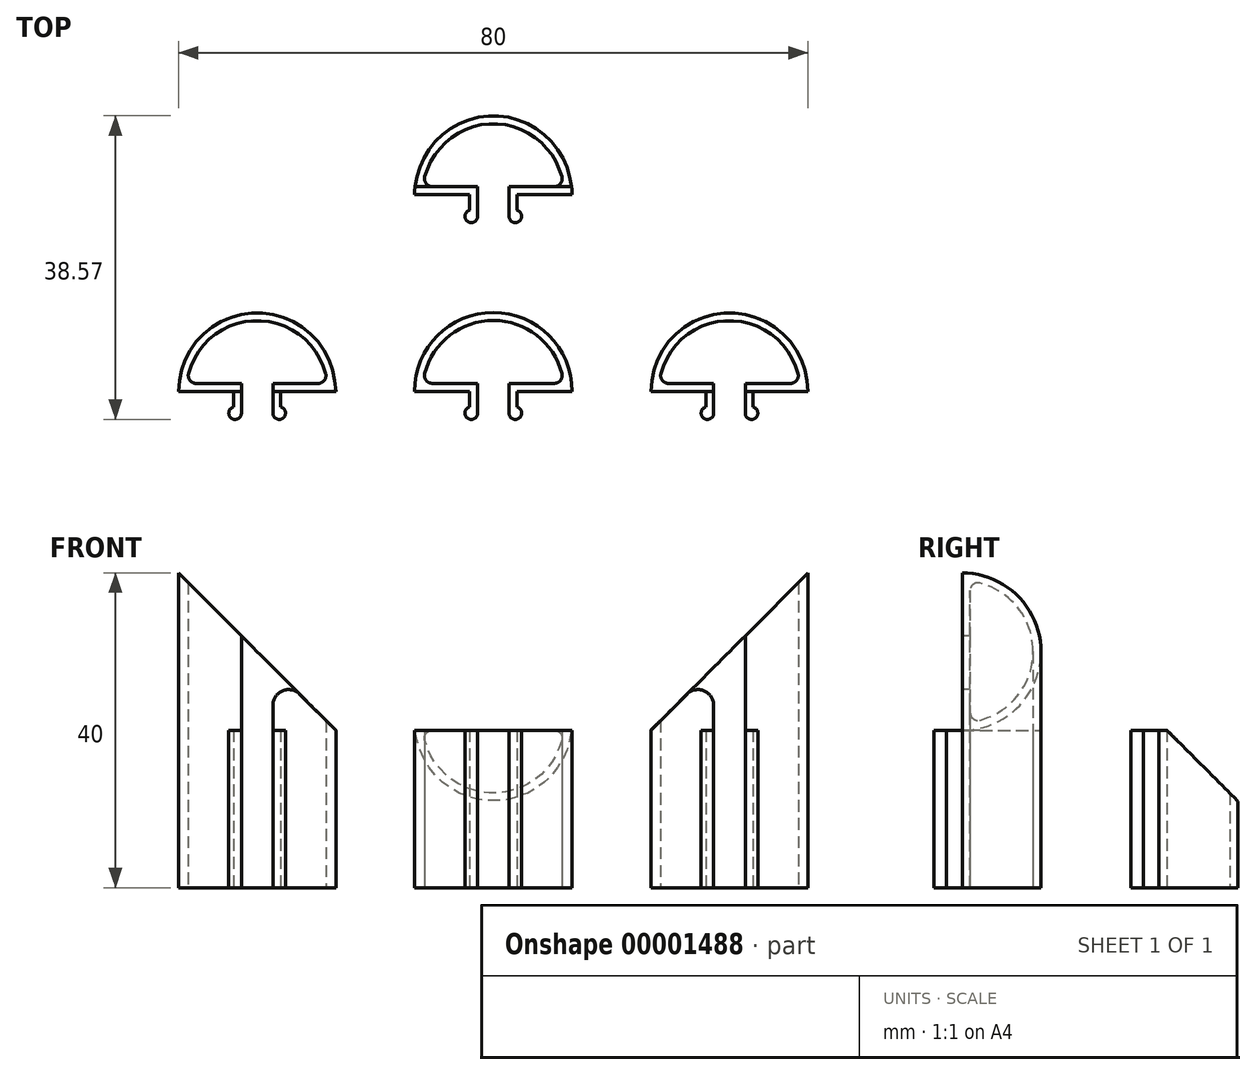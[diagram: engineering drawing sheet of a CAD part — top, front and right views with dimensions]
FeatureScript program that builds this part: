
annotation { "Feature Type Name" : "Feature", "Feature Type Description" : "" }
export const myFeature = defineFeature(function(context is Context, id is Id, definition is map)
    precondition{}
    {
        {
            var Q0;
            Q0=qCreatedBy(makeId("Top.planeOp"),FACE);
            var sketch = newSketch(context, id + "F0", { "sketchPlane" : qUnion([Q0])});
            skLineSegment(sketch, "E0", {"start": v(-3, 0) * mm, "end": v(-10, 0) * mm});
            skLineSegment(sketch, "E1", {"start": v(3, 0) * mm, "end": v(10, 0) * mm});
            skLineSegment(sketch, "E2", {"start": v(-3, 0) * mm, "end": v(-3, -2) * mm});
            skLineSegment(sketch, "E3", {"start": v(3, -2) * mm, "end": v(3, 0) * mm});
            skArc(sketch, "E4", {"start": v(10, 0) * mm, "mid": v(0, 10) * mm, "end": v(-10, 0) * mm});
            skLineSegment(sketch, "E5.0", {"start": v(-2, 1) * mm, "end": v(-2, -2.77) * mm});
            skLineSegment(sketch, "E5.1", {"start": v(-2, 1) * mm, "end": v(-8.94, 1) * mm});
            skArc(sketch, "E5.2", {"start": v(8.94, 1) * mm, "mid": v(0, 9) * mm, "end": v(-8.94, 1) * mm});
            skLineSegment(sketch, "E5.3", {"start": v(2, 1) * mm, "end": v(8.94, 1) * mm});
            skLineSegment(sketch, "E5.4", {"start": v(2, -2.77) * mm, "end": v(2, 1) * mm});
            skArc(sketch, "E6", {"start": v(-2, -2.77) * mm, "mid": v(-3.29, -3.4) * mm, "end": v(-3, -2) * mm});
            skArc(sketch, "E7", {"start": v(2, -2.77) * mm, "mid": v(3.29, -3.4) * mm, "end": v(3, -2) * mm});
            skLineSegment(sketch, "E8", {"start": v(-2.8, -2.77) * mm, "end": v(-3.6, -2.77) * mm, "construction": true});
            skLineSegment(sketch, "E9", {"start": v(2.8, -2.77) * mm, "end": v(3.6, -2.77) * mm, "construction": true});
            skSolve(sketch);
        }
        {
            var Q0;
            Q0 = qSketchRegion(id + "F0", true);
            extrude(context, id + "F1", {"entities" : qUnion([Q0]), "depth" : 20 * mm});
        }
        {
            var Q0;
            Q0=makeQuery(id+"F1.opExtrude","SWEPT_BODY",BODY,{"disambiguationData":[OSD([sQuery(id+"F0.wireOp",EDGE,"E0"),sQuery(id+"F0.wireOp",EDGE,"E1"),sQuery(id+"F0.wireOp",EDGE,"E2"),sQuery(id+"F0.wireOp",EDGE,"E3"),sQuery(id+"F0.wireOp",EDGE,"E4"),sQuery(id+"F0.wireOp",EDGE,"E5.0"),sQuery(id+"F0.wireOp",EDGE,"E5.1"),sQuery(id+"F0.wireOp",EDGE,"E5.2"),sQuery(id+"F0.wireOp",EDGE,"E5.3"),sQuery(id+"F0.wireOp",EDGE,"E5.4"),sQuery(id+"F0.wireOp",EDGE,"E6"),sQuery(id+"F0.wireOp",EDGE,"E7")])]});
            transform(context, id + "F2", {"entities" : qUnion([Q0]), "transformType" : TransformType.TRANSLATION_3D, "dx" : 30 * mm, "dy" : 0 * mm, "dz" : 0 * mm, "makeCopy" : true});
        }
        {
            var Q0;
            Q0=makeQuery(id+"F2.opPattern","COPY",FACE,{"derivedFrom":makeQuery(id+"F1.opExtrude","CAP_FACE",FACE,{"disambiguationData":[OSD([sQuery(id+"F0.wireOp",EDGE,"E0"),sQuery(id+"F0.wireOp",EDGE,"E1"),sQuery(id+"F0.wireOp",EDGE,"E2"),sQuery(id+"F0.wireOp",EDGE,"E3"),sQuery(id+"F0.wireOp",EDGE,"E4"),sQuery(id+"F0.wireOp",EDGE,"E5.0"),sQuery(id+"F0.wireOp",EDGE,"E5.1"),sQuery(id+"F0.wireOp",EDGE,"E5.2"),sQuery(id+"F0.wireOp",EDGE,"E5.3"),sQuery(id+"F0.wireOp",EDGE,"E5.4"),sQuery(id+"F0.wireOp",EDGE,"E6"),sQuery(id+"F0.wireOp",EDGE,"E7")])],"isStart":false}),"instanceName":"1"});
            var sketch = newSketch(context, id + "F3", { "sketchPlane" : qUnion([Q0])});
            skLineSegment(sketch, "E10", {"start": v(20, 0) * mm, "end": v(28, 0) * mm});
            skLineSegment(sketch, "E11", {"start": v(28, 0) * mm, "end": v(28, 1) * mm});
            skLineSegment(sketch, "E12", {"start": v(40, 0) * mm, "end": v(32, 0) * mm});
            skLineSegment(sketch, "E13", {"start": v(32, 0) * mm, "end": v(32, 1) * mm});
            skLineSegment(sketch, "E14.0", {"start": v(28, 1) * mm, "end": v(21.06, 1) * mm});
            skArc(sketch, "E15.0", {"start": v(38.94, 1) * mm, "mid": v(30, 9) * mm, "end": v(21.06, 1) * mm});
            skArc(sketch, "E16.0", {"start": v(40, 0) * mm, "mid": v(30, 10) * mm, "end": v(20, 0) * mm});
            skLineSegment(sketch, "E17.0", {"start": v(32, 1) * mm, "end": v(38.94, 1) * mm});
            skSolve(sketch);
        }
        {
            var Q0;
            Q0 = qSketchRegion(id + "F3", true);
            extrude(context, id + "F4", {"entities" : qUnion([Q0]), "operationType" : NewBodyOperationType.ADD, "depth" : 20 * mm});
        }
        {
            var Q0;
            Q0=makeQuery(id+"F4.boolean.opBoolean","MERGE",FACE,{"derivedFrom":[makeQuery(id+"F2.opPattern","COPY",FACE,{"derivedFrom":makeQuery(id+"F1.opExtrude","SWEPT_FACE",FACE,{"disambiguationData":[OSD([sQuery(id+"F0.wireOp",EDGE,"E1")])]}),"instanceName":"1"}),makeQuery(id+"F4.opExtrude","SWEPT_FACE",FACE,{"disambiguationData":[OSD([sQuery(id+"F3.wireOp",EDGE,"E12")])]})]});
            var sketch = newSketch(context, id + "F5", { "sketchPlane" : qUnion([Q0])});
            skLineSegment(sketch, "E18", {"start": v(40, 40) * mm, "end": v(20, 40) * mm});
            skLineSegment(sketch, "E19", {"start": v(20, 40) * mm, "end": v(20, 20) * mm});
            skLineSegment(sketch, "E20", {"start": v(20, 20) * mm, "end": v(40, 40) * mm});
            skSolve(sketch);
        }
        {
            var Q0;
            Q0 = qSketchRegion(id + "F5", true);
            extrude(context, id + "F6", {"entities" : qUnion([Q0]), "operationType" : NewBodyOperationType.REMOVE, "endBound" : BoundingType.THROUGH_ALL, "oppositeDirection" : true, "depth" : 25 * mm});
        }
        {
            var Q0;
            Q0=makeQuery(id+"F2.opPattern","COPY",BODY,{"derivedFrom":makeQuery(id+"F1.opExtrude","SWEPT_BODY",BODY,{"disambiguationData":[OSD([sQuery(id+"F0.wireOp",EDGE,"E0"),sQuery(id+"F0.wireOp",EDGE,"E1"),sQuery(id+"F0.wireOp",EDGE,"E2"),sQuery(id+"F0.wireOp",EDGE,"E3"),sQuery(id+"F0.wireOp",EDGE,"E4"),sQuery(id+"F0.wireOp",EDGE,"E5.0"),sQuery(id+"F0.wireOp",EDGE,"E5.1"),sQuery(id+"F0.wireOp",EDGE,"E5.2"),sQuery(id+"F0.wireOp",EDGE,"E5.3"),sQuery(id+"F0.wireOp",EDGE,"E5.4"),sQuery(id+"F0.wireOp",EDGE,"E6"),sQuery(id+"F0.wireOp",EDGE,"E7")])]}),"instanceName":"1"});
            var Q1;
            Q1=qCreatedBy(makeId("Right.planeOp"),FACE);
            mirror(context, id + "F7", {"entities" : qUnion([Q0]), "mirrorPlane" : qUnion([Q1])});
        }
        {
            var Q0;
            Q0=makeQuery(id+"F1.opExtrude","SWEPT_BODY",BODY,{"disambiguationData":[OSD([sQuery(id+"F0.wireOp",EDGE,"E0"),sQuery(id+"F0.wireOp",EDGE,"E1"),sQuery(id+"F0.wireOp",EDGE,"E2"),sQuery(id+"F0.wireOp",EDGE,"E3"),sQuery(id+"F0.wireOp",EDGE,"E4"),sQuery(id+"F0.wireOp",EDGE,"E5.0"),sQuery(id+"F0.wireOp",EDGE,"E5.1"),sQuery(id+"F0.wireOp",EDGE,"E5.2"),sQuery(id+"F0.wireOp",EDGE,"E5.3"),sQuery(id+"F0.wireOp",EDGE,"E5.4"),sQuery(id+"F0.wireOp",EDGE,"E6"),sQuery(id+"F0.wireOp",EDGE,"E7")])]});
            transform(context, id + "F8", {"entities" : qUnion([Q0]), "transformType" : TransformType.TRANSLATION_3D, "dx" : 0 * mm, "dy" : 25 * mm, "dz" : 0 * mm, "makeCopy" : true});
        }
        {
            var Q0;
            Q0=makeQuery(id+"F8.opPattern","COPY",FACE,{"derivedFrom":makeQuery(id+"F1.opExtrude","SWEPT_FACE",FACE,{"disambiguationData":[OSD([sQuery(id+"F0.wireOp",EDGE,"E5.0")])]}),"instanceName":"1"});
            var Q1;
            Q1=makeQuery(id+"F8.opPattern","COPY",FACE,{"derivedFrom":makeQuery(id+"F1.opExtrude","SWEPT_FACE",FACE,{"disambiguationData":[OSD([sQuery(id+"F0.wireOp",EDGE,"E5.4")])]}),"instanceName":"1"});
            cPlane(context, id + "F9", {"entities" : qUnion([Q0, Q1]), "cplaneType" : CPlaneType.MID_PLANE, "offset" : 150 * mm, "width" : 150 * mm, "height" : 150 * mm});
        }
        {
            var Q0;
            Q0=qCreatedBy(id+"F9.planeOp",FACE);
            var sketch = newSketch(context, id + "F10", { "sketchPlane" : qUnion([Q0])});
            skLineSegment(sketch, "E21.0", {"start": v(26, 20) * mm, "end": v(22.23, 20) * mm, "construction": true});
            skLineSegment(sketch, "E22", {"start": v(35, 20) * mm, "end": v(35, 0) * mm, "construction": true});
            skLineSegment(sketch, "E23", {"start": v(26, 20) * mm, "end": v(35, 20) * mm});
            skLineSegment(sketch, "E24", {"start": v(35, 11) * mm, "end": v(26, 20) * mm});
            skLineSegment(sketch, "E25", {"start": v(35, 20) * mm, "end": v(35, 11) * mm});
            skSolve(sketch);
        }
        {
            var Q0;
            Q0 = qSketchRegion(id + "F10", true);
            extrude(context, id + "F11", {"entities" : qUnion([Q0]), "operationType" : NewBodyOperationType.REMOVE, "endBound" : BoundingType.THROUGH_ALL, "oppositeDirection" : true, "depth" : 25 * mm, "hasSecondDirection" : true, "secondDirectionBound" : BoundingType.THROUGH_ALL, "secondDirectionOppositeDirection" : false, "secondDirectionDepth" : 25 * mm});
        }
        {
            var Q0;
            Q0=makeQuery(id+"F8.opPattern","COPY",EDGE,{"derivedFrom":makeQuery(id+"F1.opExtrude","SWEPT_EDGE",EDGE,{"disambiguationData":[OSD([sQuery(id+"F0.wireOp",EDGE,"E5.2"),sQuery(id+"F0.wireOp",EDGE,"E5.3")])]}),"instanceName":"1"});
            var Q1;
            Q1=makeQuery(id+"F8.opPattern","COPY",EDGE,{"derivedFrom":makeQuery(id+"F1.opExtrude","SWEPT_EDGE",EDGE,{"disambiguationData":[OSD([sQuery(id+"F0.wireOp",EDGE,"E5.1"),sQuery(id+"F0.wireOp",EDGE,"E5.2")])]}),"instanceName":"1"});
            var Q2;
            Q2=makeQuery(id+"F7.opPattern","COPY",EDGE,{"derivedFrom":makeQuery(id+"F4.boolean.opBoolean","MERGE",EDGE,{"derivedFrom":[makeQuery(id+"F2.opPattern","COPY",EDGE,{"derivedFrom":makeQuery(id+"F1.opExtrude","SWEPT_EDGE",EDGE,{"disambiguationData":[OSD([sQuery(id+"F0.wireOp",EDGE,"E5.2"),sQuery(id+"F0.wireOp",EDGE,"E5.3")])]}),"instanceName":"1"}),makeQuery(id+"F4.opExtrude","SWEPT_EDGE",EDGE,{"disambiguationData":[OSD([sQuery(id+"F3.wireOp",EDGE,"E15.0"),sQuery(id+"F3.wireOp",EDGE,"E17.0")])]})]}),"instanceName":"1"});
            var Q3;
            Q3=makeQuery(id+"F7.opPattern","COPY",EDGE,{"derivedFrom":makeQuery(id+"F4.boolean.opBoolean","MERGE",EDGE,{"derivedFrom":[makeQuery(id+"F2.opPattern","COPY",EDGE,{"derivedFrom":makeQuery(id+"F1.opExtrude","SWEPT_EDGE",EDGE,{"disambiguationData":[OSD([sQuery(id+"F0.wireOp",EDGE,"E5.1"),sQuery(id+"F0.wireOp",EDGE,"E5.2")])]}),"instanceName":"1"}),makeQuery(id+"F4.opExtrude","SWEPT_EDGE",EDGE,{"disambiguationData":[OSD([sQuery(id+"F3.wireOp",EDGE,"E14.0"),sQuery(id+"F3.wireOp",EDGE,"E15.0")])]})]}),"instanceName":"1"});
            var Q4;
            Q4=makeQuery(id+"F1.opExtrude","SWEPT_EDGE",EDGE,{"disambiguationData":[OSD([sQuery(id+"F0.wireOp",EDGE,"E5.2"),sQuery(id+"F0.wireOp",EDGE,"E5.3")])]});
            var Q5;
            Q5=makeQuery(id+"F1.opExtrude","SWEPT_EDGE",EDGE,{"disambiguationData":[OSD([sQuery(id+"F0.wireOp",EDGE,"E5.1"),sQuery(id+"F0.wireOp",EDGE,"E5.2")])]});
            var Q6;
            Q6=makeQuery(id+"F4.boolean.opBoolean","MERGE",EDGE,{"derivedFrom":[makeQuery(id+"F2.opPattern","COPY",EDGE,{"derivedFrom":makeQuery(id+"F1.opExtrude","SWEPT_EDGE",EDGE,{"disambiguationData":[OSD([sQuery(id+"F0.wireOp",EDGE,"E5.2"),sQuery(id+"F0.wireOp",EDGE,"E5.3")])]}),"instanceName":"1"}),makeQuery(id+"F4.opExtrude","SWEPT_EDGE",EDGE,{"disambiguationData":[OSD([sQuery(id+"F3.wireOp",EDGE,"E15.0"),sQuery(id+"F3.wireOp",EDGE,"E17.0")])]})]});
            var Q7;
            Q7=makeQuery(id+"F4.boolean.opBoolean","MERGE",EDGE,{"derivedFrom":[makeQuery(id+"F2.opPattern","COPY",EDGE,{"derivedFrom":makeQuery(id+"F1.opExtrude","SWEPT_EDGE",EDGE,{"disambiguationData":[OSD([sQuery(id+"F0.wireOp",EDGE,"E5.1"),sQuery(id+"F0.wireOp",EDGE,"E5.2")])]}),"instanceName":"1"}),makeQuery(id+"F4.opExtrude","SWEPT_EDGE",EDGE,{"disambiguationData":[OSD([sQuery(id+"F3.wireOp",EDGE,"E14.0"),sQuery(id+"F3.wireOp",EDGE,"E15.0")])]})]});
            fillet(context, id + "F12", {"entities" : qUnion([Q0, Q1, Q2, Q3, Q4, Q5, Q6, Q7]), "radius" : 1 * mm, "tangentPropagation" : true, "allowEdgeOverflow" : false});
        }
        {
            var Q0;
            Q0=makeQuery(id+"F6.boolean.opBoolean","INTERSECT",EDGE,{"derivedFrom":[makeQuery(id+"F4.boolean.opBoolean","MERGE",FACE,{"derivedFrom":[makeQuery(id+"F2.opPattern","COPY",FACE,{"derivedFrom":makeQuery(id+"F1.opExtrude","SWEPT_FACE",FACE,{"disambiguationData":[OSD([sQuery(id+"F0.wireOp",EDGE,"E5.0")])]}),"instanceName":"1"}),makeQuery(id+"F4.opExtrude","SWEPT_FACE",FACE,{"disambiguationData":[OSD([sQuery(id+"F3.wireOp",EDGE,"E11")])]})]}),makeQuery(id+"F6.opExtrude","SWEPT_FACE",FACE,{"disambiguationData":[OSD([sQuery(id+"F5.wireOp",EDGE,"E20")])]})]});
            var Q1;
            Q1=makeQuery(id+"F7.opPattern","COPY",EDGE,{"derivedFrom":makeQuery(id+"F6.boolean.opBoolean","INTERSECT",EDGE,{"derivedFrom":[makeQuery(id+"F4.boolean.opBoolean","MERGE",FACE,{"derivedFrom":[makeQuery(id+"F2.opPattern","COPY",FACE,{"derivedFrom":makeQuery(id+"F1.opExtrude","SWEPT_FACE",FACE,{"disambiguationData":[OSD([sQuery(id+"F0.wireOp",EDGE,"E5.0")])]}),"instanceName":"1"}),makeQuery(id+"F4.opExtrude","SWEPT_FACE",FACE,{"disambiguationData":[OSD([sQuery(id+"F3.wireOp",EDGE,"E11")])]})]}),makeQuery(id+"F6.opExtrude","SWEPT_FACE",FACE,{"disambiguationData":[OSD([sQuery(id+"F5.wireOp",EDGE,"E20")])]})]}),"instanceName":"1"});
            fillet(context, id + "F13", {"entities" : qUnion([Q0, Q1]), "radius" : 2 * mm, "tangentPropagation" : true, "allowEdgeOverflow" : false});
        }
    });
